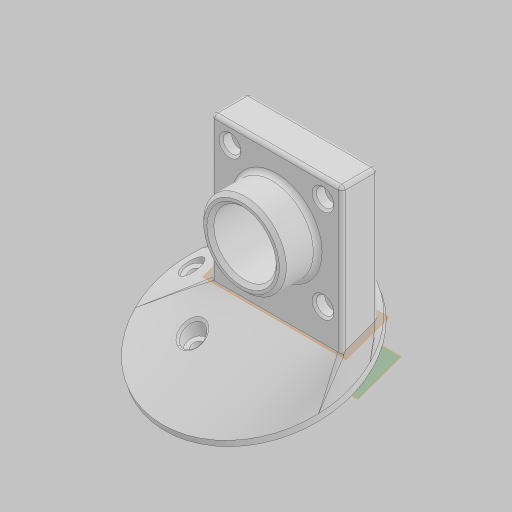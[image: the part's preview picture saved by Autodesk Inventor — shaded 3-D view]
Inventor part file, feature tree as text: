
AUTODESK INVENTOR PART (.ipt)
format: ipt  version: 2023.5 (Build 275446000, 446)  size: 459,264 bytes
history: native  units: in
note: dims shown in document units (in); Inventor stores cm internally (conversion verified against a paired STEP export)
features: extrude x7, hole x3, fillet x3, other x3, projected_geometry x3, plane x2, chamfer x2, loft x1, sketch x1, revolve x1
ambient origin geometry x8: Origin, YZ Plane, XZ Plane, XY Plane, X Axis, Y Axis, Z Axis, Center Point
bodies: Solid1 (feature_tree)
feature tree (26):
  extrude  "Extrusion1"  Depth=0.15in
  extrude  "Extrusion2"  Depth=0.15in TaperAngle=0.0deg
  plane  "Work Plane1"
  extrude  "Extrusion3"  Depth=0.15in
  loft  "Loft1"
  extrude  "Extrusion4"  Depth=0.15in
  hole  "Hole1"  [1 undecoded]
  extrude  "Extrusion5"  Depth=0.15in TaperAngle=0.0deg
  extrude  "Extrusion6"  TaperAngle=0.0deg  [1 undecoded]
  hole  "Hole2"  [1 undecoded]
  plane  "Work Plane2"
  hole  "Hole3"  [1 undecoded]
  fillet  "Fillet1"  Radius=0.3in
  chamfer  "Chamfer1"  Distance=1.1875in
  fillet  "Fillet2"  Radius=0.5in
  extrude  "Extrusion7"  Depth=0.15in
  fillet  "Fillet3"  Radius=1.3386in
  chamfer  "Chamfer2"  Distance=0.15in
  other  "Edges1"
  other  "Edges2"
  projected_geometry  "Projected Loop1"
  projected_geometry  "Projected Loop2"
  sketch  "Sketch11"  dims[d0=1.875in d1=0.525in d2=1.875in d3=0.0in d4=0.481in d5=1.875in d6=0.0in d7=0.6in d9=2.75in d10=0.1in d11=0.0in d12=0.0in d13=90.0deg d14=0.0in d15=90.0deg d16=1.6in d17=0.3in d18=0.0in d19=0.9in d20=0.75in d21=0.119in d22=0.25in d23=0.6871in d24=1.0in d25=0.8108in d26=1.1875in d27=0.5in d28=0.0in d29=0.1839in d30=1.3386in d31=0.15in d32=0.0in d33=0.094in d34=0.75in d35=0.251in d36=0.15in d37=0.6871in d38=1.0in d39=0.8108in d40=0.9792in d41=0.9792in d42=315.0deg d45=0.177in d46=0.75in d47=0.313in d48=0.45in d49=0.5635in d50=1.0in d51=0.8108in d52=0.05in d53=0.05in d54=0.125in d55=45.0deg d56=0.0625in d57=1.0in d58=1.0in d59=0.0in d60=0.25in d61=0.0312in d62=0.125in d63=45.0deg d64=0.2405in d65=90.0deg]
  other  "Srf1"
  revolve  "RevolutionSrf1"  [1 undecoded]
  projected_geometry  "Project Cut Edges1"
note: 5 required parameter values undecoded (feature->parameter linkage not recoverable at this tier; creation-order binding heuristic only, values carry confidence <= 0.55)